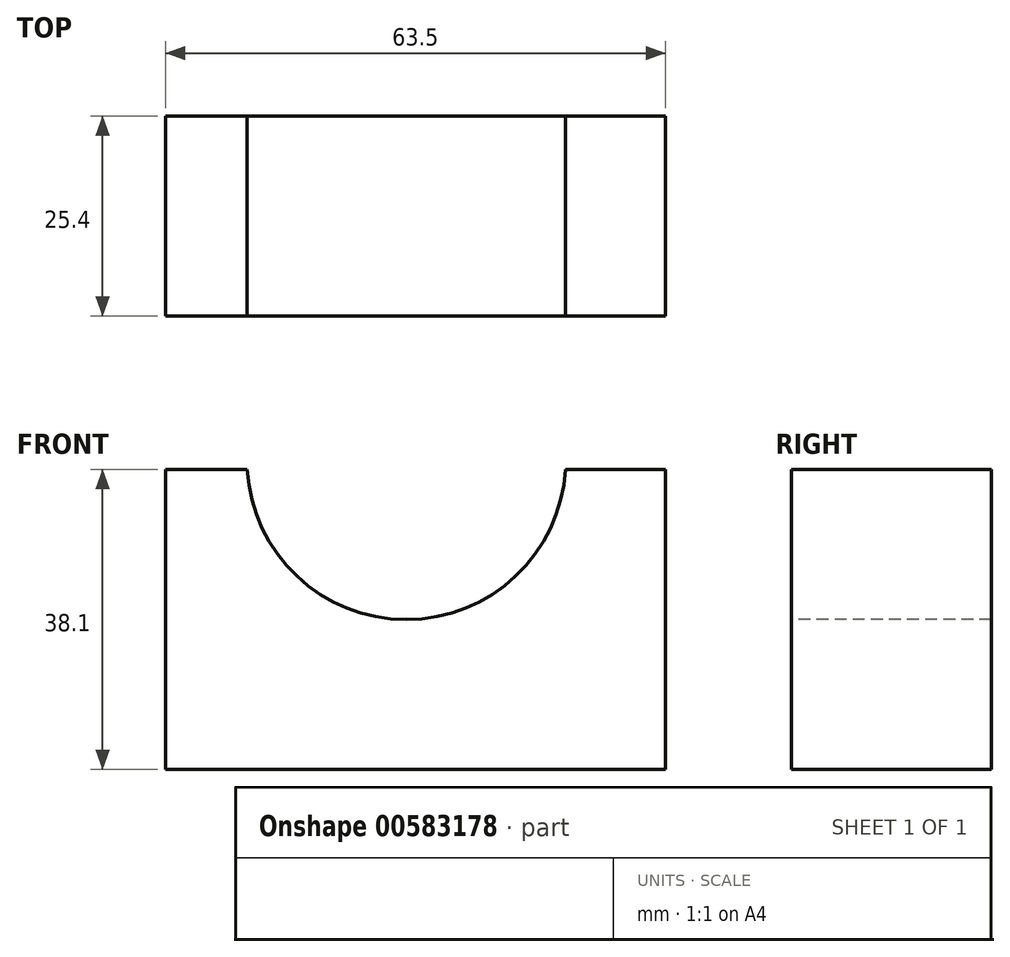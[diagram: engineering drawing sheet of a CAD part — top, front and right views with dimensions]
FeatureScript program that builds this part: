
annotation { "Feature Type Name" : "Feature", "Feature Type Description" : "" }
export const myFeature = defineFeature(function(context is Context, id is Id, definition is map)
    precondition{}
    {
        {
            var Q0;
            Q0=qCreatedBy(makeId("Front.planeOp"),FACE);
            var sketch = newSketch(context, id + "F0", { "sketchPlane" : qUnion([Q0])});
            skLineSegment(sketch, "E0.bottom", {"start": v(-63.5, 38.1) * mm, "end": v(0, 38.1) * mm});
            skLineSegment(sketch, "E0.top", {"start": v(-63.5, 0) * mm, "end": v(0, 0) * mm});
            skLineSegment(sketch, "E0.left", {"start": v(-63.5, 38.1) * mm, "end": v(-63.5, 0) * mm});
            skLineSegment(sketch, "E0.right", {"start": v(0, 38.1) * mm, "end": v(0, 0) * mm});
            skSolve(sketch);
        }
        {
            var Q0;
            Q0 = qSketchRegion(id + "F0", true);
            var Q1;
            Q1=makeQuery(id+"F0.imprint","IMPRINT",FACE,{"disambiguationData":[TD([[makeQuery(id+"F0.imprint","IMPRINT",EDGE,{"derivedFrom":sQuery(id+"F0.wireOp",EDGE,"E0.bottom")}),-1.0]])]});
            extrude(context, id + "F1", {"entities" : qUnion([Q0, Q1]), "depth" : 25.4 * mm, "offsetDistance" : 25.4 * mm});
        }
        {
            var Q0;
            Q0=makeQuery(id+"F1.opExtrude","CAP_FACE",FACE,{"disambiguationData":[OSD([sQuery(id+"F0.wireOp",EDGE,"E0.bottom"),sQuery(id+"F0.wireOp",EDGE,"E0.top"),sQuery(id+"F0.wireOp",EDGE,"E0.left"),sQuery(id+"F0.wireOp",EDGE,"E0.right")])],"isStart":false});
            var sketch = newSketch(context, id + "F2", { "sketchPlane" : qUnion([Q0])});
            skLineSegment(sketch, "E1", {"start": v(-63.5, 38.1) * mm, "end": v(-53.13, 38.1) * mm});
            skLineSegment(sketch, "E2", {"start": v(0, 38.1) * mm, "end": v(-12.7, 38.1) * mm});
            skCircle(sketch, "E3", {"center": v(-32.92, 39.28) * mm, "radius": 20.25 * mm});
            skPoint(sketch, "E3.third.point", {"position": v(-12.7, 38.1) * mm});
            skSolve(sketch);
        }
        {
            var Q0;
            {var subQ0=sQuery(id+"F2.wireOp",EDGE,"E3");var subQ1=makeQuery(id+"F1.opExtrude","CAP_EDGE",EDGE,{"disambiguationData":[OSD([sQuery(id+"F0.wireOp",EDGE,"E0.bottom")])],"isStart":false});var subQ2=makeQuery(id+"F2.imprint","INTERSECT",VERTEX,{"derivedFrom":[subQ1,sQuery(id+"F2.wireOp",EDGE,"E1"),subQ0]});Q0=makeQuery(id+"F2.imprint","IMPRINT",FACE,{"disambiguationData":[TD([[makeQuery(id+"F2.imprint","IMPRINT",EDGE,{"disambiguationData":[TD([[subQ2,-1.0]])],"derivedFrom":subQ0}),1.0]])]});}
            extrude(context, id + "F3", {"entities" : qUnion([Q0]), "operationType" : NewBodyOperationType.REMOVE, "endBound" : BoundingType.THROUGH_ALL, "oppositeDirection" : true, "depth" : 25.4 * mm, "offsetDistance" : 25.4 * mm});
        }
    });
